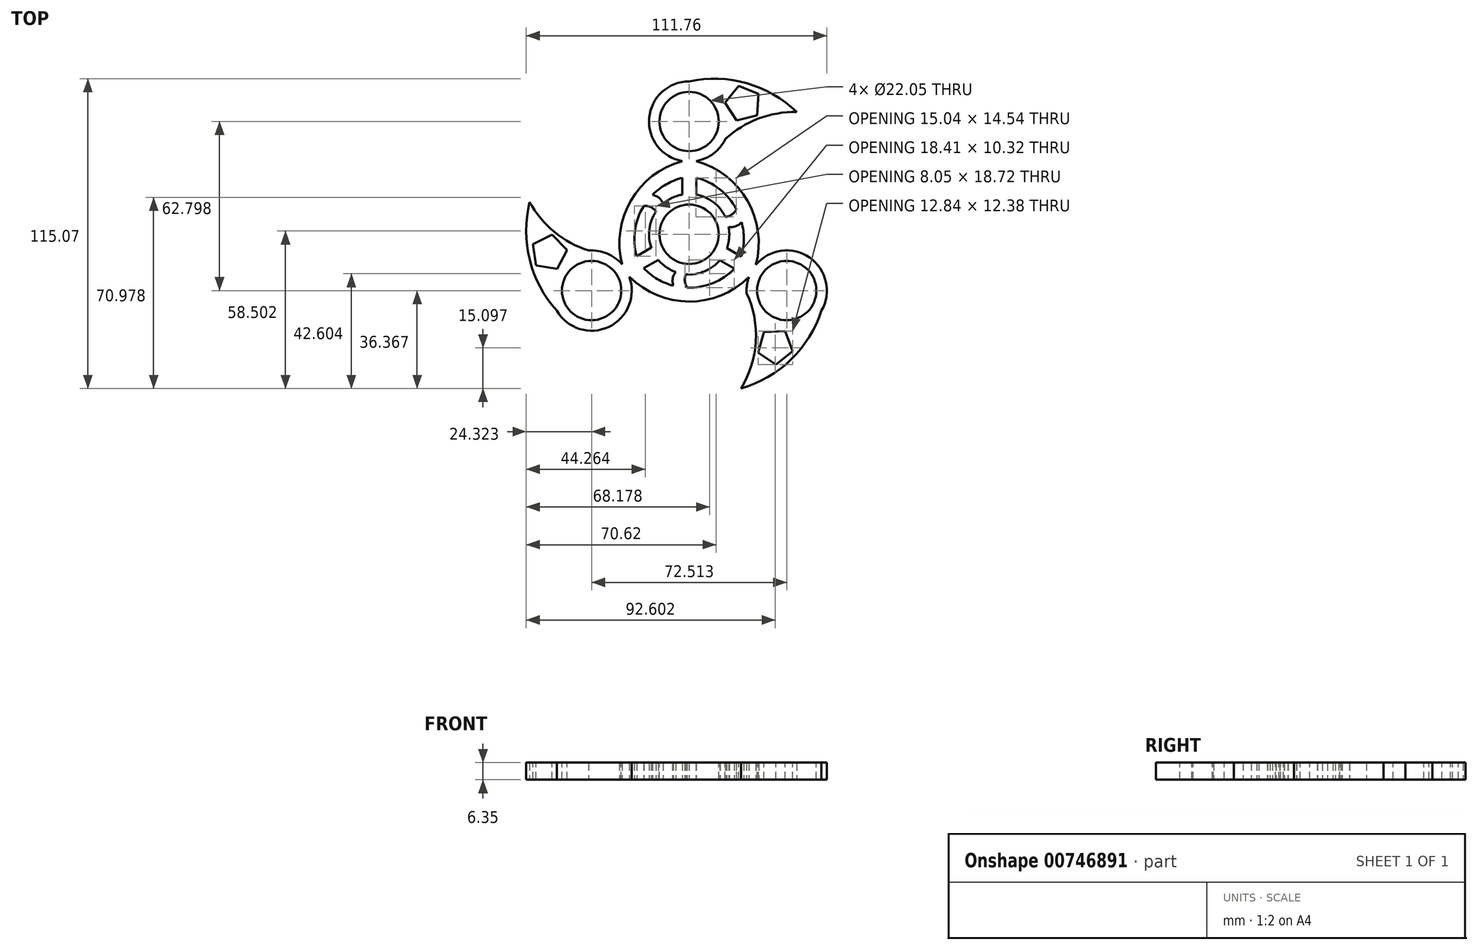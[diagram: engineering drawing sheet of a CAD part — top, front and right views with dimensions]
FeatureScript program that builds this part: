
annotation { "Feature Type Name" : "Feature", "Feature Type Description" : "" }
export const myFeature = defineFeature(function(context is Context, id is Id, definition is map)
    precondition{}
    {
        {
            var Q0;
            Q0=qCreatedBy(makeId("Top.planeOp"),FACE);
            var sketch = newSketch(context, id + "F0", { "sketchPlane" : qUnion([Q0])});
            skCircle(sketch, "E0", {"center": v(0, 0) * mm, "radius": 14.92 * mm});
            skLineSegment(sketch, "E1.bottom", {"start": v(-2.52, 14.7) * mm, "end": v(2.67, 14.7) * mm});
            skLineSegment(sketch, "E1.top", {"start": v(-2.52, 27.4) * mm, "end": v(2.67, 27.4) * mm});
            skLineSegment(sketch, "E1.left", {"start": v(-2.52, 14.7) * mm, "end": v(-2.52, 27.4) * mm});
            skLineSegment(sketch, "E1.right", {"start": v(2.67, 14.7) * mm, "end": v(2.67, 27.4) * mm});
            skCircle(sketch, "E2", {"center": v(0, 41.87) * mm, "radius": 14.92 * mm});
            skArc(sketch, "E3", {"start": v(39.97, 45.37) * mm, "mid": v(21.4, 56.06) * mm, "end": v(0, 56.79) * mm});
            skArc(sketch, "E4", {"start": v(39.97, 45.37) * mm, "mid": v(22.11, 41.38) * mm, "end": v(8.25, 29.43) * mm});
            skCircle(sketch, "E5.1.1", {"center": v(-36.26, -20.93) * mm, "radius": 14.92 * mm});
            skLineSegment(sketch, "E5.1.2", {"start": v(-11.48, -9.54) * mm, "end": v(-22.48, -15.89) * mm});
            skLineSegment(sketch, "E5.1.3", {"start": v(-14.07, -5.04) * mm, "end": v(-25.07, -11.39) * mm});
            skArc(sketch, "E5.1.5", {"start": v(-59.28, 11.93) * mm, "mid": v(-59.26, -9.5) * mm, "end": v(-49.18, -28.4) * mm});
            skArc(sketch, "E5.1.6", {"start": v(-59.28, 11.93) * mm, "mid": v(-46.89, -1.54) * mm, "end": v(-29.61, -7.57) * mm});
            skLineSegment(sketch, "E5.1.7", {"start": v(-22.48, -15.89) * mm, "end": v(-25.07, -11.39) * mm});
            skLineSegment(sketch, "E5.1.8", {"start": v(-11.48, -9.54) * mm, "end": v(-14.07, -5.04) * mm});
            skCircle(sketch, "E5.2.1", {"center": v(36.26, -20.93) * mm, "radius": 14.92 * mm});
            skLineSegment(sketch, "E5.2.2", {"start": v(14, -5.17) * mm, "end": v(25, -11.52) * mm});
            skLineSegment(sketch, "E5.2.3", {"start": v(11.4, -9.67) * mm, "end": v(22.4, -16.02) * mm});
            skArc(sketch, "E5.2.5", {"start": v(19.3, -57.3) * mm, "mid": v(37.85, -46.57) * mm, "end": v(49.18, -28.4) * mm});
            skArc(sketch, "E5.2.6", {"start": v(19.3, -57.3) * mm, "mid": v(24.78, -39.84) * mm, "end": v(21.36, -21.86) * mm});
            skLineSegment(sketch, "E5.2.7", {"start": v(25, -11.52) * mm, "end": v(22.4, -16.02) * mm});
            skLineSegment(sketch, "E5.2.8", {"start": v(14, -5.17) * mm, "end": v(11.4, -9.67) * mm});
            skSolve(sketch);
        }
        {
            var Q0;
            {var subQ0=sQuery(id+"F0.wireOp",EDGE,"E3");Q0=makeQuery(id+"F0.imprint","IMPRINT",FACE,{"disambiguationData":[TD([[makeQuery(id+"F0.imprint","IMPRINT",EDGE,{"derivedFrom":subQ0}),1.0]])]});}
            var Q1;
            {var subQ1=sQuery(id+"F0.wireOp",EDGE,"E0");var subQ3=sQuery(id+"F0.wireOp",EDGE,"E1.bottom");var subQ4=makeQuery(id+"F0.imprint","INTERSECT",VERTEX,{"derivedFrom":[subQ3,subQ1]});Q1=makeQuery(id+"F0.imprint","IMPRINT",FACE,{"disambiguationData":[TD([[makeQuery(id+"F0.imprint","IMPRINT",EDGE,{"disambiguationData":[TD([[subQ4,1.0]])],"derivedFrom":subQ3}),-1.0]])]});}
            var Q2;
            {var subQ0=sQuery(id+"F0.wireOp",EDGE,"E5.1.5");Q2=makeQuery(id+"F0.imprint","IMPRINT",FACE,{"disambiguationData":[TD([[makeQuery(id+"F0.imprint","IMPRINT",EDGE,{"derivedFrom":subQ0}),1.0]])]});}
            var Q3;
            {var subQ3=sQuery(id+"F0.wireOp",EDGE,"E5.2.1");var subQ5=sQuery(id+"F0.wireOp",EDGE,"E5.2.2");var subQ8=makeQuery(id+"F0.imprint","INTERSECT",VERTEX,{"derivedFrom":[subQ3,subQ5]});Q3=makeQuery(id+"F0.imprint","IMPRINT",FACE,{"disambiguationData":[TD([[makeQuery(id+"F0.imprint","IMPRINT",EDGE,{"disambiguationData":[TD([[subQ8,-1.0]])],"derivedFrom":subQ3}),-1.0]])]});}
            var Q4;
            {var subQ0=sQuery(id+"F0.wireOp",EDGE,"E1.right");var subQ1=sQuery(id+"F0.wireOp",EDGE,"E1.bottom");var subQ2=makeQuery(id+"F0.imprint","INTERSECT",VERTEX,{"derivedFrom":[subQ1,subQ0]});Q4=makeQuery(id+"F0.imprint","IMPRINT",FACE,{"disambiguationData":[TD([[makeQuery(id+"F0.imprint","IMPRINT",EDGE,{"disambiguationData":[TD([[subQ2,1.0]])],"derivedFrom":subQ1}),1.0]])]});}
            var Q5;
            {var subQ5=sQuery(id+"F0.wireOp",EDGE,"E5.1.1");var subQ7=sQuery(id+"F0.wireOp",EDGE,"E5.1.2");var subQ9=makeQuery(id+"F0.imprint","INTERSECT",VERTEX,{"derivedFrom":[subQ5,subQ7]});Q5=makeQuery(id+"F0.imprint","IMPRINT",FACE,{"disambiguationData":[TD([[makeQuery(id+"F0.imprint","IMPRINT",EDGE,{"disambiguationData":[TD([[subQ9,-1.0]])],"derivedFrom":subQ5}),-1.0]])]});}
            var Q6;
            {var subQ1=sQuery(id+"F0.wireOp",EDGE,"E1.top");Q6=makeQuery(id+"F0.imprint","IMPRINT",FACE,{"disambiguationData":[TD([[makeQuery(id+"F0.imprint","IMPRINT",EDGE,{"derivedFrom":subQ1}),1.0]])]});}
            var Q7;
            {var subQ0=sQuery(id+"F0.wireOp",EDGE,"E5.2.5");Q7=makeQuery(id+"F0.imprint","IMPRINT",FACE,{"disambiguationData":[TD([[makeQuery(id+"F0.imprint","IMPRINT",EDGE,{"derivedFrom":subQ0}),1.0]])]});}
            var Q8;
            {var subQ0=sQuery(id+"F0.wireOp",EDGE,"E5.1.7");Q8=makeQuery(id+"F0.imprint","IMPRINT",FACE,{"disambiguationData":[TD([[makeQuery(id+"F0.imprint","IMPRINT",EDGE,{"derivedFrom":subQ0}),1.0]])]});}
            var Q9;
            {var subQ0=sQuery(id+"F0.wireOp",EDGE,"E5.2.7");Q9=makeQuery(id+"F0.imprint","IMPRINT",FACE,{"disambiguationData":[TD([[makeQuery(id+"F0.imprint","IMPRINT",EDGE,{"derivedFrom":subQ0}),1.0]])]});}
            var Q10;
            {var subQ0=sQuery(id+"F0.wireOp",EDGE,"E4");var subQ1=sQuery(id+"F0.wireOp",EDGE,"E2");var subQ2=makeQuery(id+"F0.imprint","INTERSECT",VERTEX,{"disambiguationData":[OD(0.0)],"derivedFrom":[subQ1,subQ0]});Q10=makeQuery(id+"F0.imprint","IMPRINT",FACE,{"disambiguationData":[TD([[makeQuery(id+"F0.imprint","IMPRINT",EDGE,{"disambiguationData":[TD([[subQ2,-1.0]])],"derivedFrom":subQ1}),1.0]])]});}
            var Q11;
            {var subQ0=sQuery(id+"F0.wireOp",EDGE,"E5.1.6");var subQ1=sQuery(id+"F0.wireOp",EDGE,"E5.1.1");var subQ2=makeQuery(id+"F0.imprint","INTERSECT",VERTEX,{"disambiguationData":[OD(0.0)],"derivedFrom":[subQ1,subQ0]});Q11=makeQuery(id+"F0.imprint","IMPRINT",FACE,{"disambiguationData":[TD([[makeQuery(id+"F0.imprint","IMPRINT",EDGE,{"disambiguationData":[TD([[subQ2,-1.0]])],"derivedFrom":subQ1}),1.0]])]});}
            var Q12;
            {var subQ0=sQuery(id+"F0.wireOp",EDGE,"E5.2.6");var subQ1=sQuery(id+"F0.wireOp",EDGE,"E5.2.1");var subQ2=makeQuery(id+"F0.imprint","INTERSECT",VERTEX,{"disambiguationData":[OD(0.0)],"derivedFrom":[subQ1,subQ0]});Q12=makeQuery(id+"F0.imprint","IMPRINT",FACE,{"disambiguationData":[TD([[makeQuery(id+"F0.imprint","IMPRINT",EDGE,{"disambiguationData":[TD([[subQ2,-1.0]])],"derivedFrom":subQ1}),1.0]])]});}
            var Q13;
            {var subQ5=sQuery(id+"F0.wireOp",EDGE,"E5.2.7");Q13=makeQuery(id+"F0.imprint","IMPRINT",FACE,{"disambiguationData":[TD([[makeQuery(id+"F0.imprint","IMPRINT",EDGE,{"derivedFrom":subQ5}),-1.0]])]});}
            var Q14;
            {var subQ5=sQuery(id+"F0.wireOp",EDGE,"E5.1.7");Q14=makeQuery(id+"F0.imprint","IMPRINT",FACE,{"disambiguationData":[TD([[makeQuery(id+"F0.imprint","IMPRINT",EDGE,{"derivedFrom":subQ5}),-1.0]])]});}
            var Q15;
            {var subQ0=sQuery(id+"F0.wireOp",EDGE,"E0");var subQ1=sQuery(id+"F0.wireOp",EDGE,"E1.bottom");var subQ3=makeQuery(id+"F0.imprint","INTERSECT",VERTEX,{"derivedFrom":[subQ1,subQ0]});Q15=makeQuery(id+"F0.imprint","IMPRINT",FACE,{"disambiguationData":[TD([[makeQuery(id+"F0.imprint","IMPRINT",EDGE,{"disambiguationData":[TD([[subQ3,1.0]])],"derivedFrom":subQ1}),1.0]])]});}
            var Q16;
            {var subQ0=sQuery(id+"F0.wireOp",EDGE,"E0");var subQ1=sQuery(id+"F0.wireOp",EDGE,"E5.1.8");var subQ3=makeQuery(id+"F0.imprint","INTERSECT",VERTEX,{"derivedFrom":[subQ1,subQ0]});Q16=makeQuery(id+"F0.imprint","IMPRINT",FACE,{"disambiguationData":[TD([[makeQuery(id+"F0.imprint","IMPRINT",EDGE,{"disambiguationData":[TD([[subQ3,1.0]])],"derivedFrom":subQ1}),1.0]])]});}
            var Q17;
            {var subQ0=sQuery(id+"F0.wireOp",EDGE,"E1.top");Q17=makeQuery(id+"F0.imprint","IMPRINT",FACE,{"disambiguationData":[TD([[makeQuery(id+"F0.imprint","IMPRINT",EDGE,{"derivedFrom":subQ0}),-1.0]])]});}
            var Q18;
            {var subQ0=sQuery(id+"F0.wireOp",EDGE,"E5.2.8");var subQ1=sQuery(id+"F0.wireOp",EDGE,"E0");var subQ3=makeQuery(id+"F0.imprint","INTERSECT",VERTEX,{"derivedFrom":[subQ1,subQ0]});Q18=makeQuery(id+"F0.imprint","IMPRINT",FACE,{"disambiguationData":[TD([[makeQuery(id+"F0.imprint","IMPRINT",EDGE,{"disambiguationData":[TD([[subQ3,-1.0]])],"derivedFrom":subQ1}),1.0]])]});}
            extrude(context, id + "F1", {"entities" : qUnion([Q0, Q1, Q2, Q3, Q4, Q5, Q6, Q7, Q8, Q9, Q10, Q11, Q12, Q13, Q14, Q15, Q16, Q17, Q18]), "depth" : 6.35 * mm, "offsetDistance" : 25.4 * mm});
        }
        {
            var Q0;
            Q0=makeQuery(id+"F1.opExtrude","CAP_FACE",FACE,{"disambiguationData":[OSD([sQuery(id+"F0.wireOp",EDGE,"E1.bottom"),sQuery(id+"F0.wireOp",EDGE,"E1.left"),sQuery(id+"F0.wireOp",EDGE,"E1.right"),sQuery(id+"F0.wireOp",EDGE,"E2"),sQuery(id+"F0.wireOp",EDGE,"E3"),sQuery(id+"F0.wireOp",EDGE,"E4"),sQuery(id+"F0.wireOp",EDGE,"E5.1.1"),sQuery(id+"F0.wireOp",EDGE,"E5.1.2"),sQuery(id+"F0.wireOp",EDGE,"E5.1.3"),sQuery(id+"F0.wireOp",EDGE,"E5.1.5"),sQuery(id+"F0.wireOp",EDGE,"E5.1.6"),sQuery(id+"F0.wireOp",EDGE,"E5.1.8"),sQuery(id+"F0.wireOp",EDGE,"E0"),sQuery(id+"F0.wireOp",EDGE,"E5.2.1"),sQuery(id+"F0.wireOp",EDGE,"E5.2.2"),sQuery(id+"F0.wireOp",EDGE,"E5.2.3"),sQuery(id+"F0.wireOp",EDGE,"E5.2.5"),sQuery(id+"F0.wireOp",EDGE,"E5.2.6"),sQuery(id+"F0.wireOp",EDGE,"E5.2.8")])],"isStart":false});
            var sketch = newSketch(context, id + "F2", { "sketchPlane" : qUnion([Q0])});
            skCircle(sketch, "E6", {"center": v(0, 41.87) * mm, "radius": 11.02 * mm});
            skCircle(sketch, "E7", {"center": v(36.26, -20.93) * mm, "radius": 11.02 * mm});
            skCircle(sketch, "E8", {"center": v(-36.26, -20.93) * mm, "radius": 11.02 * mm});
            skSolve(sketch);
        }
        {
            var Q0;
            Q0 = qSketchRegion(id + "F2", true);
            extrude(context, id + "F3", {"entities" : qUnion([Q0]), "operationType" : NewBodyOperationType.REMOVE, "oppositeDirection" : true, "depth" : 25.4 * mm, "offsetDistance" : 25.4 * mm});
        }
        {
            var Q0;
            Q0=makeQuery(id+"F1.opExtrude","CAP_FACE",FACE,{"disambiguationData":[OSD([sQuery(id+"F0.wireOp",EDGE,"E1.bottom"),sQuery(id+"F0.wireOp",EDGE,"E1.left"),sQuery(id+"F0.wireOp",EDGE,"E1.right"),sQuery(id+"F0.wireOp",EDGE,"E2"),sQuery(id+"F0.wireOp",EDGE,"E3"),sQuery(id+"F0.wireOp",EDGE,"E4"),sQuery(id+"F0.wireOp",EDGE,"E5.1.1"),sQuery(id+"F0.wireOp",EDGE,"E5.1.2"),sQuery(id+"F0.wireOp",EDGE,"E5.1.3"),sQuery(id+"F0.wireOp",EDGE,"E5.1.5"),sQuery(id+"F0.wireOp",EDGE,"E5.1.6"),sQuery(id+"F0.wireOp",EDGE,"E5.1.8"),sQuery(id+"F0.wireOp",EDGE,"E0"),sQuery(id+"F0.wireOp",EDGE,"E5.2.1"),sQuery(id+"F0.wireOp",EDGE,"E5.2.2"),sQuery(id+"F0.wireOp",EDGE,"E5.2.3"),sQuery(id+"F0.wireOp",EDGE,"E5.2.5"),sQuery(id+"F0.wireOp",EDGE,"E5.2.6"),sQuery(id+"F0.wireOp",EDGE,"E5.2.8")])],"isStart":false});
            var sketch = newSketch(context, id + "F4", { "sketchPlane" : qUnion([Q0])});
            skCircle(sketch, "E9", {"center": v(0, 0) * mm, "radius": 11.02 * mm});
            skSolve(sketch);
        }
        {
            var Q0;
            Q0 = qSketchRegion(id + "F4", true);
            extrude(context, id + "F5", {"entities" : qUnion([Q0]), "operationType" : NewBodyOperationType.REMOVE, "oppositeDirection" : true, "depth" : 25.4 * mm, "offsetDistance" : 25.4 * mm});
        }
        {
            var Q0;
            Q0=qCreatedBy(makeId("Top.planeOp"),FACE);
            var sketch = newSketch(context, id + "F6", { "sketchPlane" : qUnion([Q0])});
            skArc(sketch, "E10", {"start": v(-2.52, 27.16) * mm, "mid": v(-21.62, 12.55) * mm, "end": v(-24.88, -11.28) * mm});
            skArc(sketch, "E11", {"start": v(-2.52, 20.93) * mm, "mid": v(-17.18, 9.99) * mm, "end": v(-19.48, -8.16) * mm});
            skLineSegment(sketch, "E12", {"start": v(-2.52, 20.93) * mm, "end": v(-2.52, 27.16) * mm});
            skLineSegment(sketch, "E13", {"start": v(-24.88, -11.28) * mm, "end": v(-19.48, -8.16) * mm});
            skLineSegment(sketch, "E14.1.0", {"start": v(-16.87, -12.65) * mm, "end": v(-22.26, -15.76) * mm});
            skArc(sketch, "E14.1.1", {"start": v(-22.26, -15.76) * mm, "mid": v(-0.06, -25) * mm, "end": v(22.2, -15.9) * mm});
            skArc(sketch, "E14.1.2", {"start": v(-16.87, -12.65) * mm, "mid": v(-0.06, -19.87) * mm, "end": v(16.8, -12.79) * mm});
            skLineSegment(sketch, "E14.1.3", {"start": v(22.2, -15.9) * mm, "end": v(16.8, -12.79) * mm});
            skLineSegment(sketch, "E14.2.0", {"start": v(19.39, -8.28) * mm, "end": v(24.78, -11.4) * mm});
            skArc(sketch, "E14.2.1", {"start": v(24.78, -11.4) * mm, "mid": v(21.68, 12.45) * mm, "end": v(2.67, 27.18) * mm});
            skArc(sketch, "E14.2.2", {"start": v(19.39, -8.28) * mm, "mid": v(17.24, 9.88) * mm, "end": v(2.67, 20.95) * mm});
            skLineSegment(sketch, "E14.2.3", {"start": v(2.67, 27.18) * mm, "end": v(2.67, 20.95) * mm});
            skPoint(sketch, "E14.center", {"position": v(0, 0) * mm});
            skSolve(sketch);
        }
        {
            var Q0;
            Q0=makeQuery(id+"F6.imprint","IMPRINT",FACE,{"disambiguationData":[TD([[makeQuery(id+"F6.imprint","IMPRINT",EDGE,{"derivedFrom":sQuery(id+"F6.wireOp",EDGE,"E10")}),1.0]])]});
            var Q1;
            Q1=makeQuery(id+"F6.imprint","IMPRINT",FACE,{"disambiguationData":[TD([[makeQuery(id+"F6.imprint","IMPRINT",EDGE,{"derivedFrom":sQuery(id+"F6.wireOp",EDGE,"E14.2.0")}),1.0]])]});
            var Q2;
            Q2=makeQuery(id+"F6.imprint","IMPRINT",FACE,{"disambiguationData":[TD([[makeQuery(id+"F6.imprint","IMPRINT",EDGE,{"derivedFrom":sQuery(id+"F6.wireOp",EDGE,"E14.1.0")}),1.0]])]});
            extrude(context, id + "F7", {"entities" : qUnion([Q0, Q1, Q2]), "operationType" : NewBodyOperationType.ADD, "depth" : 6.35 * mm, "offsetDistance" : 25.4 * mm});
        }
        {
            var Q0;
            Q0=qCreatedBy(makeId("Top.planeOp"),FACE);
            var sketch = newSketch(context, id + "F8", { "sketchPlane" : qUnion([Q0])});
            skArc(sketch, "E15", {"start": v(-9.54, 10.74) * mm, "mid": v(-11.47, 13.73) * mm, "end": v(-14.92, 14.62) * mm});
            skArc(sketch, "E16", {"start": v(-11.47, 6.87) * mm, "mid": v(-14.09, 9.99) * mm, "end": v(-18.15, 10.3) * mm});
            skPoint(sketch, "E16.startSnap0", {"position": v(-11.47, 13.73) * mm});
            skLineSegment(sketch, "E17", {"start": v(-18.15, 10.3) * mm, "end": v(-14.92, 14.62) * mm});
            skLineSegment(sketch, "E18", {"start": v(-9.54, 10.74) * mm, "end": v(-11.47, 6.87) * mm});
            skArc(sketch, "E19.1.0", {"start": v(-4.53, -13.63) * mm, "mid": v(-6.16, -16.8) * mm, "end": v(-5.2, -20.23) * mm});
            skLineSegment(sketch, "E19.1.1", {"start": v(-4.53, -13.63) * mm, "end": v(-0.21, -13.37) * mm});
            skArc(sketch, "E19.1.2", {"start": v(-0.21, -13.37) * mm, "mid": v(-1.6, -17.2) * mm, "end": v(0.15, -20.87) * mm});
            skLineSegment(sketch, "E19.1.3", {"start": v(0.15, -20.87) * mm, "end": v(-5.2, -20.23) * mm});
            skArc(sketch, "E19.2.0", {"start": v(14.07, 2.9) * mm, "mid": v(17.63, 3.07) * mm, "end": v(20.12, 5.61) * mm});
            skLineSegment(sketch, "E19.2.1", {"start": v(14.07, 2.9) * mm, "end": v(11.68, 6.5) * mm});
            skArc(sketch, "E19.2.2", {"start": v(11.68, 6.5) * mm, "mid": v(15.7, 7.2) * mm, "end": v(18, 10.56) * mm});
            skLineSegment(sketch, "E19.2.3", {"start": v(18, 10.56) * mm, "end": v(20.12, 5.61) * mm});
            skPoint(sketch, "E19.center", {"position": v(0, 0) * mm});
            skSolve(sketch);
        }
        {
            var Q0;
            Q0=makeQuery(id+"F8.imprint","IMPRINT",FACE,{"disambiguationData":[TD([[makeQuery(id+"F8.imprint","IMPRINT",EDGE,{"derivedFrom":sQuery(id+"F8.wireOp",EDGE,"E15")}),1.0]])]});
            var Q1;
            Q1=makeQuery(id+"F8.imprint","IMPRINT",FACE,{"disambiguationData":[TD([[makeQuery(id+"F8.imprint","IMPRINT",EDGE,{"derivedFrom":sQuery(id+"F8.wireOp",EDGE,"E19.2.0")}),1.0]])]});
            var Q2;
            Q2=makeQuery(id+"F8.imprint","IMPRINT",FACE,{"disambiguationData":[TD([[makeQuery(id+"F8.imprint","IMPRINT",EDGE,{"derivedFrom":sQuery(id+"F8.wireOp",EDGE,"E19.1.0")}),1.0]])]});
            extrude(context, id + "F9", {"entities" : qUnion([Q0, Q1, Q2]), "operationType" : NewBodyOperationType.ADD, "depth" : 6.35 * mm, "offsetDistance" : 25.4 * mm});
        }
        {
            var Q0;
            Q0=makeQuery(id+"F9.boolean.opBoolean","MERGE",FACE,{"derivedFrom":[makeQuery(id+"F7.boolean.opBoolean","MERGE",FACE,{"derivedFrom":[makeQuery(id+"F1.opExtrude","CAP_FACE",FACE,{"disambiguationData":[OSD([sQuery(id+"F0.wireOp",EDGE,"E1.bottom"),sQuery(id+"F0.wireOp",EDGE,"E1.left"),sQuery(id+"F0.wireOp",EDGE,"E1.right"),sQuery(id+"F0.wireOp",EDGE,"E2"),sQuery(id+"F0.wireOp",EDGE,"E3"),sQuery(id+"F0.wireOp",EDGE,"E4"),sQuery(id+"F0.wireOp",EDGE,"E5.1.1"),sQuery(id+"F0.wireOp",EDGE,"E5.1.2"),sQuery(id+"F0.wireOp",EDGE,"E5.1.3"),sQuery(id+"F0.wireOp",EDGE,"E5.1.5"),sQuery(id+"F0.wireOp",EDGE,"E5.1.6"),sQuery(id+"F0.wireOp",EDGE,"E5.1.8"),sQuery(id+"F0.wireOp",EDGE,"E0"),sQuery(id+"F0.wireOp",EDGE,"E5.2.1"),sQuery(id+"F0.wireOp",EDGE,"E5.2.2"),sQuery(id+"F0.wireOp",EDGE,"E5.2.3"),sQuery(id+"F0.wireOp",EDGE,"E5.2.5"),sQuery(id+"F0.wireOp",EDGE,"E5.2.6"),sQuery(id+"F0.wireOp",EDGE,"E5.2.8")])],"isStart":false}),makeQuery(id+"F7.opExtrude","CAP_FACE",FACE,{"disambiguationData":[OSD([sQuery(id+"F6.wireOp",EDGE,"E10"),sQuery(id+"F6.wireOp",EDGE,"E11"),sQuery(id+"F6.wireOp",EDGE,"E12"),sQuery(id+"F6.wireOp",EDGE,"E13")])],"isStart":false}),makeQuery(id+"F7.opExtrude","CAP_FACE",FACE,{"disambiguationData":[OSD([sQuery(id+"F6.wireOp",EDGE,"E14.1.0"),sQuery(id+"F6.wireOp",EDGE,"E14.1.1"),sQuery(id+"F6.wireOp",EDGE,"E14.1.2"),sQuery(id+"F6.wireOp",EDGE,"E14.1.3")])],"isStart":false}),makeQuery(id+"F7.opExtrude","CAP_FACE",FACE,{"disambiguationData":[OSD([sQuery(id+"F6.wireOp",EDGE,"E14.2.0"),sQuery(id+"F6.wireOp",EDGE,"E14.2.1"),sQuery(id+"F6.wireOp",EDGE,"E14.2.2"),sQuery(id+"F6.wireOp",EDGE,"E14.2.3")])],"isStart":false})]}),makeQuery(id+"F9.opExtrude","CAP_FACE",FACE,{"disambiguationData":[OSD([sQuery(id+"F8.wireOp",EDGE,"E15"),sQuery(id+"F8.wireOp",EDGE,"E16"),sQuery(id+"F8.wireOp",EDGE,"E17"),sQuery(id+"F8.wireOp",EDGE,"E18")])],"isStart":false}),makeQuery(id+"F9.opExtrude","CAP_FACE",FACE,{"disambiguationData":[OSD([sQuery(id+"F8.wireOp",EDGE,"E19.1.0"),sQuery(id+"F8.wireOp",EDGE,"E19.1.1"),sQuery(id+"F8.wireOp",EDGE,"E19.1.2"),sQuery(id+"F8.wireOp",EDGE,"E19.1.3")])],"isStart":false}),makeQuery(id+"F9.opExtrude","CAP_FACE",FACE,{"disambiguationData":[OSD([sQuery(id+"F8.wireOp",EDGE,"E19.2.0"),sQuery(id+"F8.wireOp",EDGE,"E19.2.1"),sQuery(id+"F8.wireOp",EDGE,"E19.2.2"),sQuery(id+"F8.wireOp",EDGE,"E19.2.3")])],"isStart":false})]});
            var sketch = newSketch(context, id + "F10", { "sketchPlane" : qUnion([Q0])});
            skCircle(sketch, "E20.cCircle", {"center": v(20.1, 48.48) * mm, "radius": 6.76 * mm, "construction": true});
            skLineSegment(sketch, "E20.0", {"start": v(17.6, 42.2) * mm, "end": v(13.35, 48.9) * mm});
            skLineSegment(sketch, "E20.1", {"start": v(13.35, 48.9) * mm, "end": v(18.41, 55.02) * mm});
            skLineSegment(sketch, "E20.2", {"start": v(18.41, 55.02) * mm, "end": v(25.8, 52.1) * mm});
            skLineSegment(sketch, "E20.3", {"start": v(25.8, 52.1) * mm, "end": v(25.3, 44.17) * mm});
            skLineSegment(sketch, "E20.4", {"start": v(25.3, 44.17) * mm, "end": v(17.6, 42.2) * mm});
            skLineSegment(sketch, "E21.1.0", {"start": v(-50.9, -0.17) * mm, "end": v(-45.34, -5.85) * mm});
            skLineSegment(sketch, "E21.1.1", {"start": v(-58.02, -3.7) * mm, "end": v(-50.9, -0.17) * mm});
            skLineSegment(sketch, "E21.1.2", {"start": v(-56.86, -11.56) * mm, "end": v(-58.02, -3.7) * mm});
            skLineSegment(sketch, "E21.1.3", {"start": v(-49.02, -12.89) * mm, "end": v(-56.86, -11.56) * mm});
            skLineSegment(sketch, "E21.1.4", {"start": v(-45.34, -5.85) * mm, "end": v(-49.02, -12.89) * mm});
            skLineSegment(sketch, "E21.2.0", {"start": v(25.6, -44) * mm, "end": v(27.74, -36.35) * mm});
            skLineSegment(sketch, "E21.2.1", {"start": v(32.22, -48.4) * mm, "end": v(25.6, -44) * mm});
            skLineSegment(sketch, "E21.2.2", {"start": v(38.44, -43.46) * mm, "end": v(32.22, -48.4) * mm});
            skLineSegment(sketch, "E21.2.3", {"start": v(35.67, -36.01) * mm, "end": v(38.44, -43.46) * mm});
            skLineSegment(sketch, "E21.2.4", {"start": v(27.74, -36.35) * mm, "end": v(35.67, -36.01) * mm});
            skPoint(sketch, "E21.center", {"position": v(0, 0) * mm});
            skSolve(sketch);
        }
        {
            var Q0;
            Q0=makeQuery(id+"F10.imprint","IMPRINT",FACE,{"disambiguationData":[TD([[makeQuery(id+"F10.imprint","IMPRINT",EDGE,{"derivedFrom":sQuery(id+"F10.wireOp",EDGE,"E21.1.0")}),-1.0]])]});
            var Q1;
            Q1=makeQuery(id+"F10.imprint","IMPRINT",FACE,{"disambiguationData":[TD([[makeQuery(id+"F10.imprint","IMPRINT",EDGE,{"derivedFrom":sQuery(id+"F10.wireOp",EDGE,"E21.2.0")}),-1.0]])]});
            var Q2;
            Q2=makeQuery(id+"F10.imprint","IMPRINT",FACE,{"disambiguationData":[TD([[makeQuery(id+"F10.imprint","IMPRINT",EDGE,{"derivedFrom":sQuery(id+"F10.wireOp",EDGE,"E20.0")}),-1.0]])]});
            extrude(context, id + "F11", {"entities" : qUnion([Q0, Q1, Q2]), "operationType" : NewBodyOperationType.REMOVE, "oppositeDirection" : true, "depth" : 25.4 * mm, "offsetDistance" : 25.4 * mm});
        }
    });
